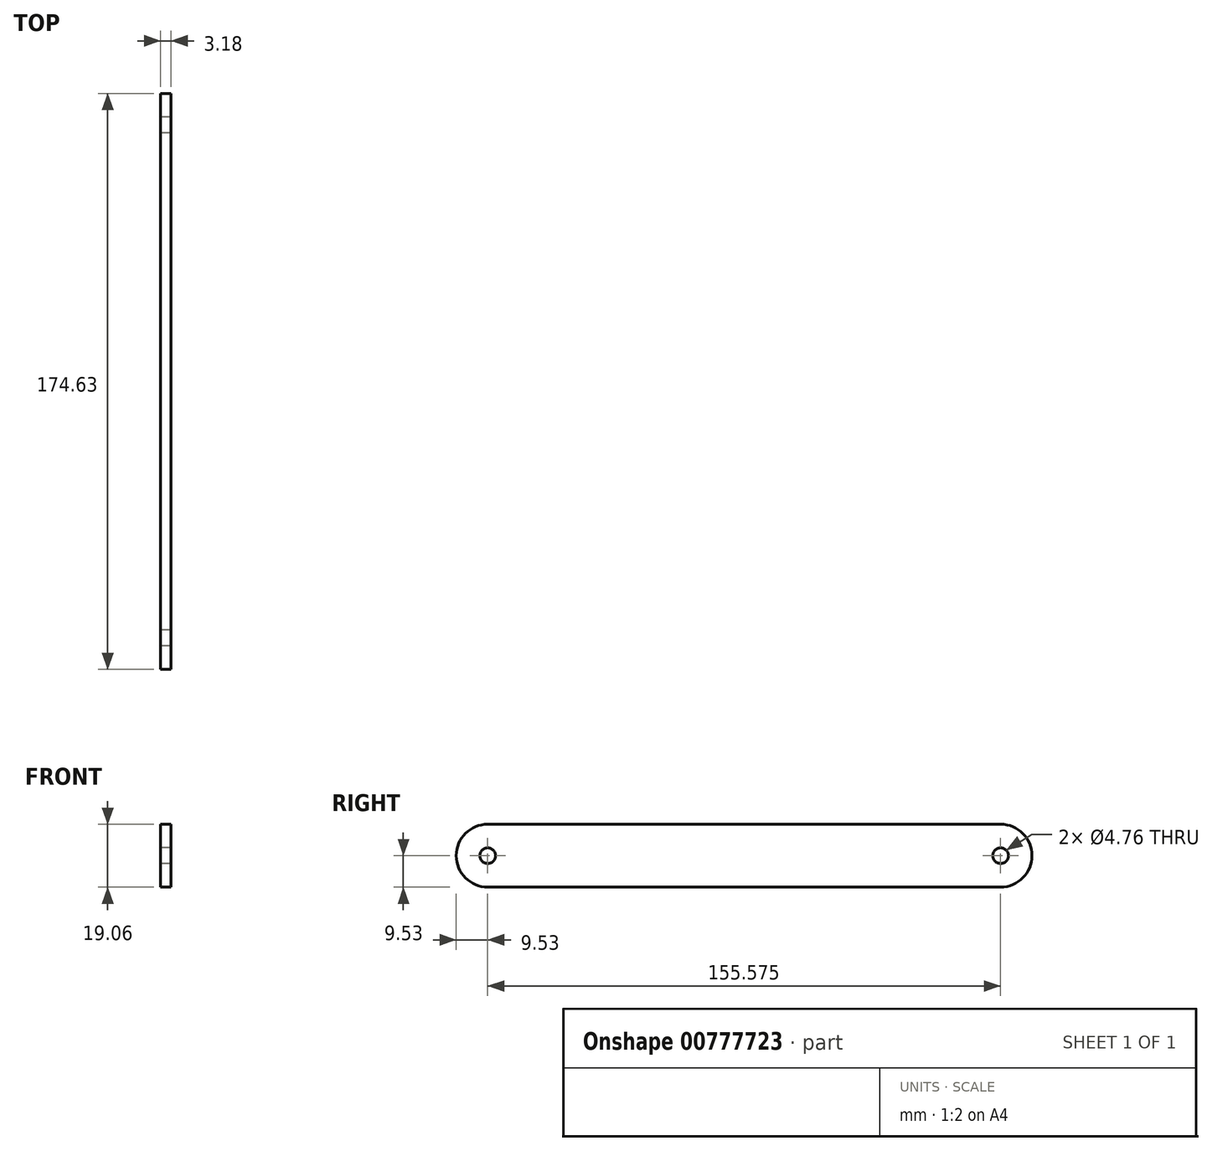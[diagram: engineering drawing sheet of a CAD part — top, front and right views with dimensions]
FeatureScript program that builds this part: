
annotation { "Feature Type Name" : "Feature", "Feature Type Description" : "" }
export const myFeature = defineFeature(function(context is Context, id is Id, definition is map)
    precondition{}
    {
        {
            var Q0;
            Q0=qCreatedBy(makeId("Right.planeOp"),FACE);
            var sketch = newSketch(context, id + "F0", { "sketchPlane" : qUnion([Q0])});
            skLineSegment(sketch, "E0.bottom", {"start": v(0, 9.53) * mm, "end": v(155.58, 9.53) * mm});
            skLineSegment(sketch, "E0.top", {"start": v(0, -9.53) * mm, "end": v(155.58, -9.53) * mm});
            skArc(sketch, "E1.filletArc", {"start": v(0, 9.53) * mm, "mid": v(-9.53, 0) * mm, "end": v(0, -9.53) * mm});
            skArc(sketch, "E2.filletArc", {"start": v(155.58, -9.53) * mm, "mid": v(165.1, 0) * mm, "end": v(155.58, 9.53) * mm});
            skCircle(sketch, "E3", {"center": v(0, 0) * mm, "radius": 2.38 * mm});
            skCircle(sketch, "E4", {"center": v(155.58, 0) * mm, "radius": 2.38 * mm});
            skSolve(sketch);
        }
        {
            var Q0;
            Q0=qSketchRegion(id+"F0",true);
            extrude(context, id + "F1", {"entities" : qUnion([Q0]), "depth" : 3.17 * mm, "offsetDistance" : 25.4 * mm});
        }
    });
